# Revit family: KDW030001
name_source: partatom
category: Plumbing Fixtures
revit_build: Autodesk Revit 2015 (Build: 20140606_1530(x64)
units: mm (PartAtom-declared; Revit-internal decimal feet)

## types (1)
- KDW030001
    Additional features of the object = https://www.kaldewei.co.uk
    BIMobject category = Bath & Spas
    Brand url = http://www.kaldewei.com
    Color = https://www.kaldewei.co.uk
    ColourOptions = https://www.kaldewei.co.uk
    Configurator link = https://www.kaldewei.co.uk
    Description details = KALDEWEI international Worldwide partner for iconic bathroom solutions made of KALDEWEI steel enamel  KALDEWEI steel enamel delivers unique advantages that inspire excellence in bathroom design. Projects across the world, from upmarket hotels to private homes, capture the sophisticated aesthetic that recommends KALDEWEI as the partner of choice. As a leading international manufacturer of high-quality shower surfaces, bathtubs and washbasins made of superior steel enamel, KALDEWEI today is present in more than 80 countries.
    Design country = Germany
    DrainSize = 52 mm
    Durability = https://EN 14516
    Edition number = 1
    Finish = https://www.kaldewei.co.uk
    IFC Classification = Furnishing Element
    IfcExportAs = BATH
    IfcExportType = IfcSanitaryTerminalType
    Link towards a photo of the product = https://www.kaldewei.co.uk
    Manufacturer country = Germany
    ManufacturerCountry = GERMANY
    ManufacturerName = KALDEWEI
    Material = steel enamel
    Material main = Steel
    Material secondary = Enamel
    NBS Reference Code = 35-06-08
    NBS Reference Description = Baths
    Name = CAYONO DUO
    Nominal height = 750 cm
    Nominal width = 1700 cm
    ObjectName = CAYONO DUO 750x1700x400
    ObjectNorm = EN 14516 EU DECLARATION OF PERFORMANCE (https://www.kaldewei.de
    Polantis code = KDW030001
    Product Guid = a56f45b6-51db-42b4-8e88-261e4862a7d3
    Product SKU = 724
    Product certification = https://www.kaldewei.co.uk
    Product data url = https://bimobject.com
    Product family = CAYONO
    Product group = Bathtub
    Product url = https://www.kaldewei.co.uk
    ProductInformation = Model No. 724: The CAYONO DUO is the first KALDEWEI duo bathtub in the ADVANTAGE segment and offers an attractive solution for two people bathing together. The CAYONO DUO’s hallmarks are lavish space, reclining comfort and a voluminous interior. Together with CAYONOPLAN showers and PURO washbasins, CAYONO bathtubs are now the new standard in the family bathroom.
    QR code = http://bimobject.com
    SerialNumber = 724
    Shape = Rectangular baths
    Size = 750x1700x400
    Sound Insulation = DIN 4109:2016, VDI4100:2012
    Sustainability = https://kaldewei-fa.secure.footprint.net
    Technical data link = https://kaldewei.typo-live.web-factory.de
    Technical description = https://www.kaldewei.co.uk
    Type of accessories = https://www.kaldewei.co.uk
    Type of support framing = https://www.kaldewei.co.uk
    UNSPSC Code = 30181501
    UNSPSCCode = 30181500
    UNSPSCNames = Sanitary ware
    URL = https://www.kaldewei.com
    Uniclass 1.4 Code = L7211
    Uniclass 1.4 Description = Baths
    Uniclass 2.0 Code = PR-35-06-08
    Uniclass 2.0 Description = Baths
    Uniclass 2015 = Pr_40_20_06_08
    Version = 2
    WarrantyDurationParts = 30
    WarrantyDurationUnit = Year
    WarrantyStartDate = https://www.kaldewei.co.uk
    WaterSupplyOverflowAndWasteHolesOverflow = 52 mm
    WaterSupplyOverflowAndWasteHolesWaste = 52 mm
    Website link = https://www.kaldewei.co.uk
    Weight Net (Kg) = 0

## geometry (parser evidence)
native form markers: Sweep x19
no freeform markers — native parametric forms only
